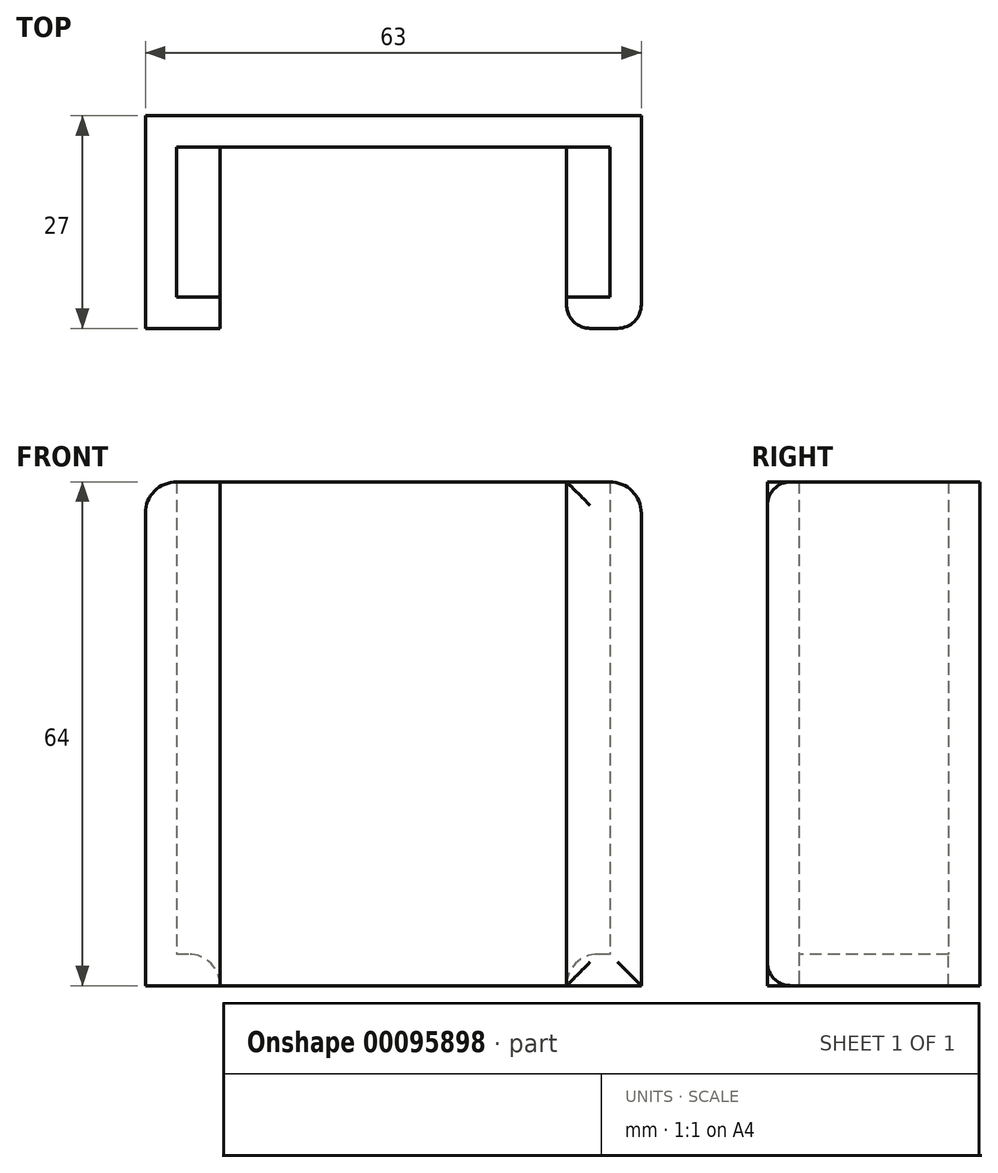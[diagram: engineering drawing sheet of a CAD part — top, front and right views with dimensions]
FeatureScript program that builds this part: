
annotation { "Feature Type Name" : "Feature", "Feature Type Description" : "" }
export const myFeature = defineFeature(function(context is Context, id is Id, definition is map)
    precondition{}
    {
        {
            var Q0;
            Q0=qCreatedBy(makeId("Top.planeOp"),FACE);
            var sketch = newSketch(context, id + "F0", { "sketchPlane" : qUnion([Q0])});
            skLineSegment(sketch, "E0.bottom", {"start": v(27.5, -9.5) * mm, "end": v(-27.5, -9.5) * mm});
            skLineSegment(sketch, "E0.top", {"start": v(27.5, 9.5) * mm, "end": v(-27.5, 9.5) * mm});
            skLineSegment(sketch, "E0.left", {"start": v(27.5, -9.5) * mm, "end": v(27.5, 9.5) * mm});
            skLineSegment(sketch, "E0.right", {"start": v(-27.5, -9.5) * mm, "end": v(-27.5, 9.5) * mm});
            skPoint(sketch, "E0.middle", {"position": v(0, 0) * mm});
            skLineSegment(sketch, "E1.bottom", {"start": v(31.5, -13.5) * mm, "end": v(-31.5, -13.5) * mm});
            skLineSegment(sketch, "E1.top", {"start": v(31.5, 13.5) * mm, "end": v(-31.5, 13.5) * mm});
            skLineSegment(sketch, "E1.left", {"start": v(31.5, -13.5) * mm, "end": v(31.5, 13.5) * mm});
            skLineSegment(sketch, "E1.right", {"start": v(-31.5, -13.5) * mm, "end": v(-31.5, 13.5) * mm});
            skSolve(sketch);
        }
        {
            var Q0;
            Q0=makeQuery(id+"F0.imprint","IMPRINT",FACE,{"disambiguationData":[TD([[makeQuery(id+"F0.imprint","IMPRINT",EDGE,{"derivedFrom":sQuery(id+"F0.wireOp",EDGE,"E0.bottom")}),1.0]])]});
            extrude(context, id + "F1", {"entities" : qUnion([Q0]), "depth" : 60 * mm});
        }
        {
            var Q0;
            Q0=makeQuery(id+"F0.imprint","IMPRINT",FACE,{"disambiguationData":[TD([[makeQuery(id+"F0.imprint","IMPRINT",EDGE,{"derivedFrom":sQuery(id+"F0.wireOp",EDGE,"E0.bottom")}),-1.0]])]});
            var Q1;
            Q1=makeQuery(id+"F0.imprint","IMPRINT",FACE,{"disambiguationData":[TD([[makeQuery(id+"F0.imprint","IMPRINT",EDGE,{"derivedFrom":sQuery(id+"F0.wireOp",EDGE,"E0.bottom")}),1.0]])]});
            extrude(context, id + "F2", {"entities" : qUnion([Q0, Q1]), "operationType" : NewBodyOperationType.ADD, "oppositeDirection" : true, "depth" : 4 * mm});
        }
        {
            var Q0;
            {var subQ0=sQuery(id+"F0.wireOp",EDGE,"E1.bottom");Q0=makeQuery(id+"F2.boolean.opBoolean","MERGE",FACE,{"derivedFrom":[makeQuery(id+"F1.opExtrude","SWEPT_FACE",FACE,{"disambiguationData":[OSD([subQ0])]}),makeQuery(id+"F2.opExtrude","SWEPT_FACE",FACE,{"disambiguationData":[OSD([subQ0])]})]});}
            var sketch = newSketch(context, id + "F3", { "sketchPlane" : qUnion([Q0])});
            skLineSegment(sketch, "E2", {"start": v(0, 60) * mm, "end": v(0, -4) * mm, "construction": true});
            skLineSegment(sketch, "E3.bottom", {"start": v(-22, 60) * mm, "end": v(22, 60) * mm});
            skLineSegment(sketch, "E3.top", {"start": v(-22, -4) * mm, "end": v(22, -4) * mm});
            skLineSegment(sketch, "E3.left", {"start": v(-22, 60) * mm, "end": v(-22, -4) * mm});
            skLineSegment(sketch, "E3.right", {"start": v(22, 60) * mm, "end": v(22, -4) * mm});
            skSolve(sketch);
        }
        {
            var Q0;
            Q0=makeQuery(id+"F3.imprint","IMPRINT",FACE,{"disambiguationData":[TD([[makeQuery(id+"F3.imprint","IMPRINT",EDGE,{"derivedFrom":sQuery(id+"F3.wireOp",EDGE,"E3.bottom")}),1.0]])]});
            extrude(context, id + "F4", {"entities" : qUnion([Q0]), "operationType" : NewBodyOperationType.REMOVE, "oppositeDirection" : true, "depth" : 23 * mm});
        }
        {
            var Q0;
            Q0=makeQuery(id+"F4.boolean.opBoolean","COPY",EDGE,{"derivedFrom":makeQuery(id+"F4.opExtrude","SWEPT_EDGE",EDGE,{"disambiguationData":[OSD([sQuery(id+"F0.wireOp",EDGE,"E1.bottom"),sQuery(id+"F3.wireOp",EDGE,"E3.bottom"),sQuery(id+"F3.wireOp",EDGE,"E3.left")])]})});
            var Q1;
            Q1=makeQuery(id+"F4.boolean.opBoolean","INTERSECT",EDGE,{"derivedFrom":[makeQuery(id+"F2.opExtrude","CAP_FACE",FACE,{"disambiguationData":[OSD([sQuery(id+"F0.wireOp",EDGE,"E1.bottom"),sQuery(id+"F0.wireOp",EDGE,"E1.top"),sQuery(id+"F0.wireOp",EDGE,"E1.left"),sQuery(id+"F0.wireOp",EDGE,"E1.right")])],"isStart":true}),makeQuery(id+"F4.opExtrude","SWEPT_FACE",FACE,{"disambiguationData":[OSD([sQuery(id+"F3.wireOp",EDGE,"E3.left")])]})]});
            var Q2;
            Q2=makeQuery(id+"F4.boolean.opBoolean","INTERSECT",EDGE,{"derivedFrom":[makeQuery(id+"F2.opExtrude","CAP_FACE",FACE,{"disambiguationData":[OSD([sQuery(id+"F0.wireOp",EDGE,"E1.bottom"),sQuery(id+"F0.wireOp",EDGE,"E1.top"),sQuery(id+"F0.wireOp",EDGE,"E1.left"),sQuery(id+"F0.wireOp",EDGE,"E1.right")])],"isStart":true}),makeQuery(id+"F4.opExtrude","SWEPT_FACE",FACE,{"disambiguationData":[OSD([sQuery(id+"F3.wireOp",EDGE,"E3.right")])]})]});
            var Q3;
            Q3=makeQuery(id+"F1.opExtrude","CAP_EDGE",EDGE,{"disambiguationData":[OSD([sQuery(id+"F0.wireOp",EDGE,"E1.right")])],"isStart":false});
            var Q4;
            Q4=makeQuery(id+"F1.opExtrude","CAP_EDGE",EDGE,{"disambiguationData":[OSD([sQuery(id+"F0.wireOp",EDGE,"E1.left")])],"isStart":false});
            var Q5;
            Q5=makeQuery(id+"F4.boolean.opBoolean","COPY",EDGE,{"derivedFrom":makeQuery(id+"F4.opExtrude","SWEPT_EDGE",EDGE,{"disambiguationData":[OSD([sQuery(id+"F0.wireOp",EDGE,"E1.bottom"),sQuery(id+"F3.wireOp",EDGE,"E3.bottom"),sQuery(id+"F3.wireOp",EDGE,"E3.right")])]})});
            fillet(context, id + "F5", {"entities" : qUnion([Q0, Q1, Q2, Q3, Q4, Q5]), "radius" : 4 * mm, "tangentPropagation" : true, "allowEdgeOverflow" : false});
        }
        {
            var Q0;
            Q0=makeQuery(id+"F4.boolean.opBoolean","COPY",EDGE,{"derivedFrom":makeQuery(id+"F4.opExtrude","CAP_EDGE",EDGE,{"disambiguationData":[OSD([sQuery(id+"F3.wireOp",EDGE,"E3.left")])],"isStart":true})});
            var Q1;
            {var subQ0=sQuery(id+"F0.wireOp",EDGE,"E1.left");var subQ3=sQuery(id+"F0.wireOp",EDGE,"E1.bottom");Q1=makeQuery(id+"F4.boolean.opBoolean","SPLIT",FACE,{"disambiguationData":[TD([makeQuery(id+"F1.opExtrude","SWEPT_FACE",FACE,{"disambiguationData":[OSD([subQ0])]})])],"derivedFrom":makeQuery(id+"F2.boolean.opBoolean","MERGE",FACE,{"derivedFrom":[makeQuery(id+"F1.opExtrude","SWEPT_FACE",FACE,{"disambiguationData":[OSD([subQ3])]}),makeQuery(id+"F2.opExtrude","SWEPT_FACE",FACE,{"disambiguationData":[OSD([subQ3])]})]})});}
            fillet(context, id + "F6", {"entities" : qUnion([Q0, Q1]), "radius" : 3 * mm, "tangentPropagation" : true, "allowEdgeOverflow" : false});
        }
    });
